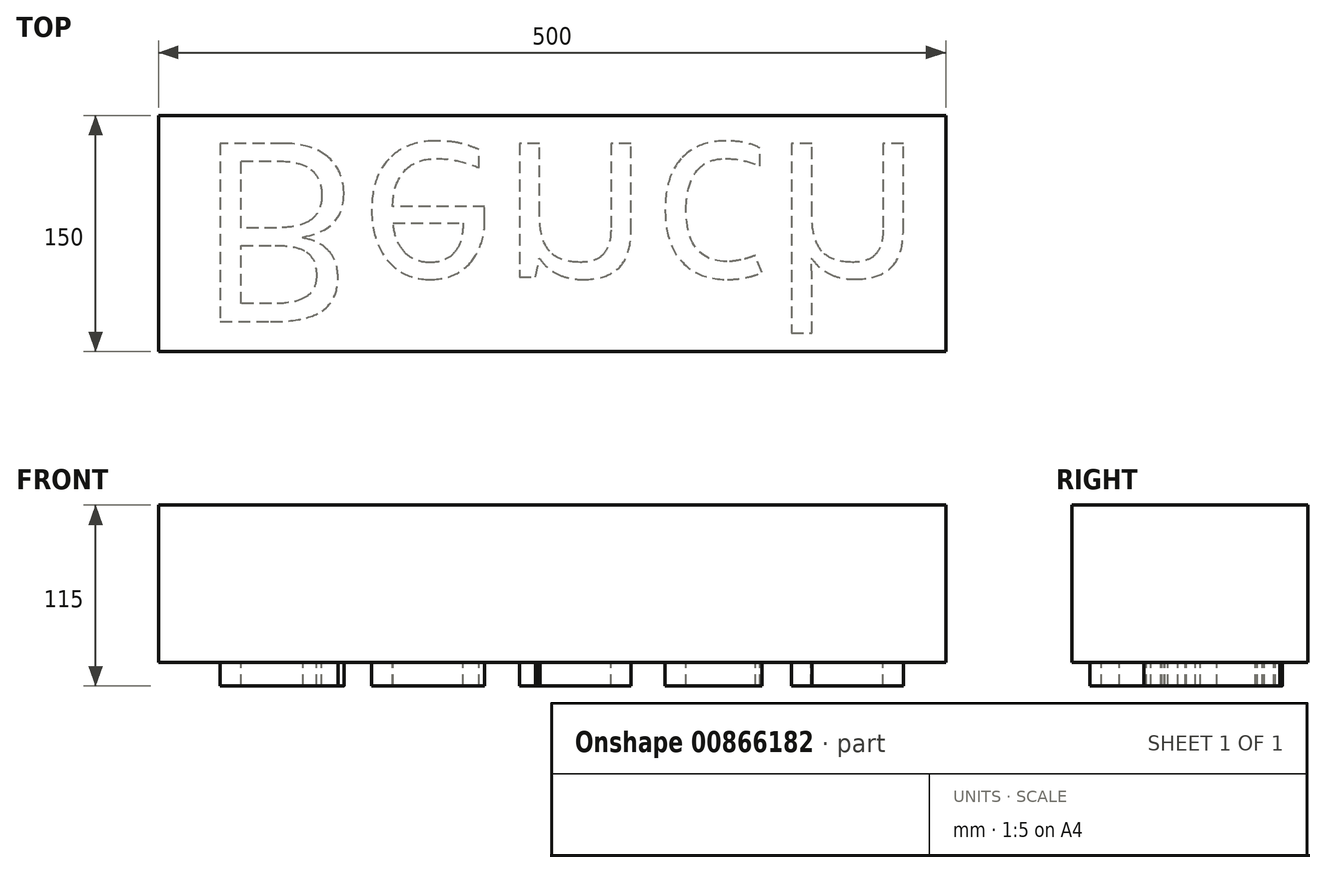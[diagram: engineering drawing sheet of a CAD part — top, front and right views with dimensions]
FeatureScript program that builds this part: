
annotation { "Feature Type Name" : "Feature", "Feature Type Description" : "" }
export const myFeature = defineFeature(function(context is Context, id is Id, definition is map)
    precondition{}
    {
        {
            var Q0;
            Q0=qCreatedBy(makeId("Front.planeOp"),FACE);
            var sketch = newSketch(context, id + "F0", { "sketchPlane" : qUnion([Q0])});
            skLineSegment(sketch, "E0.bottom", {"start": v(-209.15, 61.4) * mm, "end": v(290.85, 61.4) * mm});
            skLineSegment(sketch, "E0.top", {"start": v(-209.15, -38.6) * mm, "end": v(290.85, -38.6) * mm});
            skLineSegment(sketch, "E0.left", {"start": v(-209.15, 61.4) * mm, "end": v(-209.15, -38.6) * mm});
            skLineSegment(sketch, "E0.right", {"start": v(290.85, 61.4) * mm, "end": v(290.85, -38.6) * mm});
            skSolve(sketch);
        }
        {
            var Q0;
            Q0 = qSketchRegion(id + "F0", true);
            extrude(context, id + "F1", {"entities" : qUnion([Q0]), "depth" : 150 * mm, "offsetDistance" : 25 * mm});
        }
        {
            var Q0;
            Q0=makeQuery(id+"F1.opExtrude","SWEPT_FACE",FACE,{"disambiguationData":[OSD([sQuery(id+"F0.wireOp",EDGE,"E0.top")])]});
            var sketch = newSketch(context, id + "F2", { "sketchPlane" : qUnion([Q0])});
            skText(sketch, "E1", { "text": "Bench", "fontName": "OpenSans-Regular.ttf"});
            const initialGuessF2  = {"E1": [-0.18546, 0.01777, 1, 0, 0.11423]};
            skSetInitialGuess(sketch, initialGuessF2);
            skSolve(sketch);
        }
        {
            var Q0;
            Q0 = qSketchRegion(id + "F2", true);
            extrude(context, id + "F3", {"entities" : qUnion([Q0]), "operationType" : NewBodyOperationType.ADD, "depth" : 15 * mm, "offsetDistance" : 25 * mm});
        }
    });
